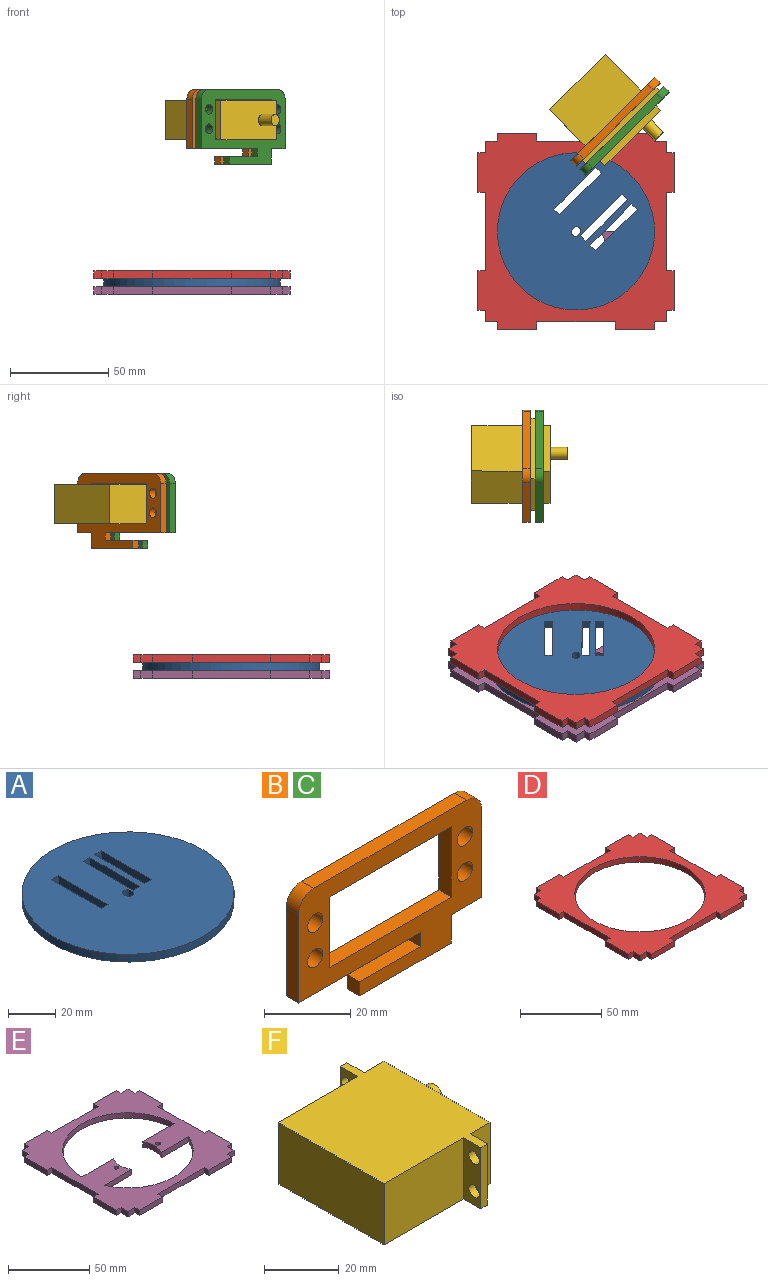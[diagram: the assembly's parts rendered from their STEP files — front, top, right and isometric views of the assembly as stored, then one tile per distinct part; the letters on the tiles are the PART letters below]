
ASSEMBLY  parts=6 mates=4
PART A: 19 faces, bbox 90x90x4 mm
  f0: plane 90x90mm, normal (0,0,1), area 5984.1mm2, adj f2,f3,f4,f5,f6,f7,f8,f9
  f1: plane 90x90mm, normal (0,0,-1), area 5984.1mm2, adj f2,f3,f4,f5,f6,f7,f8,f9
  f2: cylinder r=2.5mm len=4mm, axis (0,0,-1), area 18.5mm2, adj f0,f1,f3,f6
  f3: plane 4x3mm, normal (1,0,0), area 12mm2, adj f0,f1,f2,f4
  f4: cylinder r=2.5mm len=4mm, axis (0,0,-1), area 18.5mm2, adj f0,f1,f3,f6
  f5: cylinder r=45mm len=90mm, axis (0,0,-1), area 1131mm2, adj f0,f1
  f6: plane 4x3mm, normal (-1,0,0), area 12mm2, adj f0,f1,f2,f4
  f7: plane 4x4mm, normal (0,-1,0), area 16mm2, adj f0,f1,f8,f10
  f8: plane 30x4mm, normal (1,0,0), area 120mm2, adj f0,f1,f7,f9
  f9: plane 4x4mm, normal (0,1,0), area 16mm2, adj f0,f1,f8,f10
  f10: plane 30x4mm, normal (-1,0,0), area 120mm2, adj f0,f1,f7,f9
  f11: plane 4x4mm, normal (0,-1,0), area 16mm2, adj f0,f1,f12,f14
  f12: plane 30x4mm, normal (1,0,0), area 120mm2, adj f0,f1,f11,f13
  f13: plane 4x4mm, normal (0,1,0), area 16mm2, adj f0,f1,f12,f14
  f14: plane 30x4mm, normal (-1,0,0), area 120mm2, adj f0,f1,f11,f13
  f15: plane 30x4mm, normal (-1,0,0), area 120mm2, adj f0,f1,f16,f18
  f16: plane 4x4mm, normal (0,-1,0), area 16mm2, adj f0,f1,f15,f17
  f17: plane 30x4mm, normal (1,0,0), area 120mm2, adj f0,f1,f16,f18
  f18: plane 4x4mm, normal (0,1,0), area 16mm2, adj f0,f1,f15,f17
PART B: 22 faces, bbox 60x4x38 mm
  f0: plane 50x4mm, normal (0,0,1), area 200mm2, adj f1,f17,f20,f21
  f1: cylinder r=5mm len=5mm, axis (0,1,0), area 31.4mm2, adj f0,f2,f20,f21
  f2: plane 25x4mm, normal (-1,0,0), area 100mm2, adj f1,f3,f20,f21
  f3: plane 40x4mm, normal (0,0,-1), area 160mm2, adj f2,f4,f20,f21
  f4: plane 4x4mm, normal (-1,0,0), area 16mm2, adj f3,f5,f20,f21
  f5: plane 20x4mm, normal (0,0,1), area 80mm2, adj f4,f6,f20,f21
  f6: plane 4x4mm, normal (-1,0,0), area 16mm2, adj f5,f7,f20,f21
  f7: plane 30x4mm, normal (0,0,-1), area 120mm2, adj f6,f8,f20,f21
  f8: plane 8x4mm, normal (1,0,0), area 32mm2, adj f7,f9,f20,f21
  f9: plane 10x4mm, normal (0,0,-1), area 40mm2, adj f8,f10,f20,f21
  f10: plane 25x4mm, normal (1,0,0), area 100mm2, adj f9,f17,f20,f21
  f11: plane 20x4mm, normal (1,0,0), area 80mm2, adj f12,f18,f20,f21
  f12: plane 40x4mm, normal (0,0,-1), area 160mm2, adj f11,f13,f20,f21
  f13: plane 20x4mm, normal (-1,0,0), area 80mm2, adj f12,f18,f20,f21
  f14: cylinder r=2.5mm len=5mm, axis (0,1,0), area 62.8mm2, adj f20,f21
  f15: cylinder r=2.5mm len=5mm, axis (0,1,0), area 62.8mm2, adj f20,f21
  f16: cylinder r=2.5mm len=5mm, axis (0,1,0), area 62.8mm2, adj f20,f21
  f17: cylinder r=5mm len=5mm, axis (0,1,0), area 31.4mm2, adj f0,f10,f20,f21
  f18: plane 40x4mm, normal (0,0,1), area 160mm2, adj f11,f13,f20,f21
  f19: cylinder r=2.5mm len=5mm, axis (0,1,0), area 62.8mm2, adj f20,f21
  f20: plane 60x38mm, normal (0,-1,0), area 1070.7mm2, adj f0,f1,f2,f3,f4,f5,f6,f7
  f21: plane 60x38mm, normal (0,1,0), area 1070.7mm2, adj f0,f1,f2,f3,f4,f5,f6,f7
PART C: same geometry as B
PART D: 39 faces, bbox 100x100x4 mm
  f0: cylinder r=40mm len=80mm, axis (0,0,-1), area 1005.3mm2, adj f37,f38
  f1: plane 4x4mm, normal (0,-1,0), area 16mm2, adj f2,f36,f37,f38
  f2: plane 40x4mm, normal (-1,0,0), area 160mm2, adj f1,f3,f37,f38
  f3: plane 4x4mm, normal (0,1,0), area 16mm2, adj f2,f4,f37,f38
  f4: plane 20x4mm, normal (-1,0,0), area 80mm2, adj f3,f5,f37,f38
  f5: plane 4x4mm, normal (0,-1,0), area 16mm2, adj f4,f6,f37,f38
  f6: plane 6x4mm, normal (-1,0,0), area 24mm2, adj f5,f7,f37,f38
  f7: plane 6x4mm, normal (0,-1,0), area 24mm2, adj f6,f8,f37,f38
  f8: plane 4x4mm, normal (-1,0,0), area 16mm2, adj f7,f9,f37,f38
  f9: plane 20x4mm, normal (0,-1,0), area 80mm2, adj f8,f10,f37,f38
  f10: plane 4x4mm, normal (1,0,0), area 16mm2, adj f9,f11,f37,f38
  f11: plane 40x4mm, normal (0,-1,0), area 160mm2, adj f10,f12,f37,f38
  f12: plane 4x4mm, normal (-1,0,0), area 16mm2, adj f11,f13,f37,f38
  f13: plane 20x4mm, normal (0,-1,0), area 80mm2, adj f12,f14,f37,f38
  f14: plane 4x4mm, normal (1,0,0), area 16mm2, adj f13,f15,f37,f38
  f15: plane 6x4mm, normal (0,-1,0), area 24mm2, adj f14,f16,f37,f38
  f16: plane 6x4mm, normal (1,0,0), area 24mm2, adj f15,f17,f37,f38
  f17: plane 4x4mm, normal (0,-1,0), area 16mm2, adj f16,f18,f37,f38
  f18: plane 20x4mm, normal (1,0,0), area 80mm2, adj f17,f19,f37,f38
  f19: plane 4x4mm, normal (0,1,0), area 16mm2, adj f18,f20,f37,f38
  f20: plane 40x4mm, normal (1,0,0), area 160mm2, adj f19,f21,f37,f38
  f21: plane 4x4mm, normal (0,-1,0), area 16mm2, adj f20,f22,f37,f38
  f22: plane 20x4mm, normal (1,0,0), area 80mm2, adj f21,f23,f37,f38
  f23: plane 4x4mm, normal (0,1,0), area 16mm2, adj f22,f24,f37,f38
  f24: plane 6x4mm, normal (1,0,0), area 24mm2, adj f23,f25,f37,f38
  f25: plane 6x4mm, normal (0,1,0), area 24mm2, adj f24,f26,f37,f38
  f26: plane 4x4mm, normal (1,0,0), area 16mm2, adj f25,f27,f37,f38
  f27: plane 20x4mm, normal (0,1,0), area 80mm2, adj f26,f28,f37,f38
  f28: plane 4x4mm, normal (-1,0,0), area 16mm2, adj f27,f29,f37,f38
  f29: plane 40x4mm, normal (0,1,0), area 160mm2, adj f28,f30,f37,f38
  f30: plane 4x4mm, normal (1,0,0), area 16mm2, adj f29,f31,f37,f38
  f31: plane 20x4mm, normal (0,1,0), area 80mm2, adj f30,f32,f37,f38
  f32: plane 4x4mm, normal (-1,0,0), area 16mm2, adj f31,f33,f37,f38
  f33: plane 6x4mm, normal (0,1,0), area 24mm2, adj f32,f34,f37,f38
  f34: plane 6x4mm, normal (-1,0,0), area 24mm2, adj f33,f35,f37,f38
  f35: plane 4x4mm, normal (0,1,0), area 16mm2, adj f34,f36,f37,f38
  f36: plane 20x4mm, normal (-1,0,0), area 80mm2, adj f1,f35,f37,f38
  f37: plane 100x100mm, normal (0,0,1), area 4077.5mm2, adj f0,f1,f2,f3,f4,f5,f6,f7
  f38: plane 100x100mm, normal (0,0,-1), area 4077.5mm2, adj f0,f1,f2,f3,f4,f5,f6,f7
PART E: 48 faces, bbox 100x100x4 mm
  f0: cylinder r=40mm len=80mm, axis (0,0,-1), area 502.7mm2, adj f1,f43,f46,f47
  f1: plane 27.31x4mm, normal (0,1,0), area 109.2mm2, adj f0,f2,f46,f47
  f2: cylinder r=15mm len=16mm, axis (0,0,-1), area 67.5mm2, adj f1,f3,f46,f47
  f3: plane 23.97x4mm, normal (0,-1,0), area 95.9mm2, adj f2,f4,f46,f47
  f4: cylinder r=40mm len=73.32mm, axis (0,0,-1), area 371mm2, adj f3,f5,f46,f47
  f5: plane 23.97x4mm, normal (0,-1,0), area 95.9mm2, adj f4,f6,f46,f47
  f6: cylinder r=15mm len=16mm, axis (0,0,-1), area 67.5mm2, adj f5,f43,f46,f47
  f7: plane 4x4mm, normal (0,-1,0), area 16mm2, adj f8,f44,f46,f47
  f8: plane 40x4mm, normal (-1,0,0), area 160mm2, adj f7,f9,f46,f47
  f9: plane 4x4mm, normal (0,1,0), area 16mm2, adj f8,f10,f46,f47
  f10: plane 20x4mm, normal (-1,0,0), area 80mm2, adj f9,f11,f46,f47
  f11: plane 4x4mm, normal (0,-1,0), area 16mm2, adj f10,f12,f46,f47
  f12: plane 6x4mm, normal (-1,0,0), area 24mm2, adj f11,f13,f46,f47
  f13: plane 6x4mm, normal (0,-1,0), area 24mm2, adj f12,f14,f46,f47
  f14: plane 4x4mm, normal (-1,0,0), area 16mm2, adj f13,f15,f46,f47
  f15: plane 20x4mm, normal (0,-1,0), area 80mm2, adj f14,f16,f46,f47
  f16: plane 4x4mm, normal (1,0,0), area 16mm2, adj f15,f17,f46,f47
  f17: plane 40x4mm, normal (0,-1,0), area 160mm2, adj f16,f18,f46,f47
  f18: plane 4x4mm, normal (-1,0,0), area 16mm2, adj f17,f19,f46,f47
  f19: plane 20x4mm, normal (0,-1,0), area 80mm2, adj f18,f20,f46,f47
  f20: plane 4x4mm, normal (1,0,0), area 16mm2, adj f19,f21,f46,f47
  f21: plane 6x4mm, normal (0,-1,0), area 24mm2, adj f20,f22,f46,f47
  f22: plane 6x4mm, normal (1,0,0), area 24mm2, adj f21,f23,f46,f47
  f23: plane 4x4mm, normal (0,-1,0), area 16mm2, adj f22,f24,f46,f47
  f24: plane 20x4mm, normal (1,0,0), area 80mm2, adj f23,f25,f46,f47
  f25: plane 4x4mm, normal (0,1,0), area 16mm2, adj f24,f26,f46,f47
  f26: plane 40x4mm, normal (1,0,0), area 160mm2, adj f25,f27,f46,f47
  f27: plane 4x4mm, normal (0,-1,0), area 16mm2, adj f26,f28,f46,f47
  f28: plane 20x4mm, normal (1,0,0), area 80mm2, adj f27,f29,f46,f47
  f29: plane 4x4mm, normal (0,1,0), area 16mm2, adj f28,f30,f46,f47
  f30: plane 6x4mm, normal (1,0,0), area 24mm2, adj f29,f31,f46,f47
  f31: plane 6x4mm, normal (0,1,0), area 24mm2, adj f30,f32,f46,f47
  f32: plane 4x4mm, normal (1,0,0), area 16mm2, adj f31,f33,f46,f47
  f33: plane 20x4mm, normal (0,1,0), area 80mm2, adj f32,f34,f46,f47
  f34: plane 4x4mm, normal (-1,0,0), area 16mm2, adj f33,f35,f46,f47
  f35: plane 40x4mm, normal (0,1,0), area 160mm2, adj f34,f36,f46,f47
  f36: plane 4x4mm, normal (1,0,0), area 16mm2, adj f35,f37,f46,f47
  f37: plane 20x4mm, normal (0,1,0), area 80mm2, adj f36,f38,f46,f47
  f38: plane 4x4mm, normal (-1,0,0), area 16mm2, adj f37,f39,f46,f47
  f39: plane 6x4mm, normal (0,1,0), area 24mm2, adj f38,f40,f46,f47
  f40: plane 6x4mm, normal (-1,0,0), area 24mm2, adj f39,f41,f46,f47
  f41: plane 4x4mm, normal (0,1,0), area 16mm2, adj f40,f44,f46,f47
  f42: cylinder r=1.5mm len=4mm, axis (0,0,-1), area 37.7mm2, adj f46,f47
  f43: plane 27.31x4mm, normal (0,1,0), area 109.2mm2, adj f0,f6,f46,f47
  f44: plane 20x4mm, normal (-1,0,0), area 80mm2, adj f7,f41,f46,f47
  f45: cylinder r=1.5mm len=4mm, axis (0,0,-1), area 37.7mm2, adj f46,f47
  f46: plane 100x100mm, normal (0,0,1), area 4852.2mm2, adj f0,f1,f2,f3,f4,f5,f6,f7
  f47: plane 100x100mm, normal (0,0,-1), area 4852.2mm2, adj f0,f1,f2,f3,f4,f5,f6,f7
PART F: 20 faces, bbox 49x53x20 mm
  f0: plane 30x20mm, normal (0,-1,0), area 600mm2, adj f6,f8,f9,f13
  f1: plane 20x6.5mm, normal (-1,0,0), area 104.9mm2, adj f3,f8,f9,f10,f11,f12
  f2: plane 20x6.5mm, normal (1,0,0), area 104.9mm2, adj f5,f8,f9,f10,f11,f12
  f3: plane 30x20mm, normal (0,1,0), area 600mm2, adj f1,f6,f8,f9
  f4: plane 40x20mm, normal (1,0,0), area 771.7mm2, adj f5,f7,f8,f9,f18
  f5: plane 20x7.5mm, normal (0,1,0), area 150mm2, adj f2,f4,f8,f9
  f6: plane 40x20mm, normal (-1,0,0), area 800mm2, adj f0,f3,f8,f9
  f7: plane 20x7.5mm, normal (0,-1,0), area 150mm2, adj f4,f8,f9,f14
  f8: plane 53x40mm, normal (0,0,1), area 1632.5mm2, adj f0,f1,f2,f3,f4,f5,f6,f7
  f9: plane 53x40mm, normal (0,0,-1), area 1632.5mm2, adj f0,f1,f2,f3,f4,f5,f6,f7
  f10: plane 20x2.5mm, normal (0,1,0), area 50mm2, adj f1,f2,f8,f9
  f11: cylinder r=2mm len=4mm, axis (1,0,0), area 31.4mm2, adj f1,f2
  f12: cylinder r=2mm len=4mm, axis (1,0,0), area 31.4mm2, adj f1,f2
  f13: plane 20x6.5mm, normal (-1,0,0), area 104.9mm2, adj f0,f8,f9,f15,f16,f17
  f14: plane 20x6.5mm, normal (1,0,0), area 104.9mm2, adj f7,f8,f9,f15,f16,f17
  f15: plane 20x2.5mm, normal (0,-1,0), area 50mm2, adj f8,f9,f13,f14
  f16: cylinder r=2mm len=4mm, axis (1,0,0), area 31.4mm2, adj f13,f14
  f17: cylinder r=2mm len=4mm, axis (1,0,0), area 31.4mm2, adj f13,f14
  f18: cylinder r=3mm len=9mm, axis (-1,0,0), area 169.6mm2, adj f4,f19
  f19: plane 6x6mm, normal (1,0,0), area 28.3mm2, adj f18
PLACE A rot(axis=(0,0,-1),45.3deg) t=(103.96,68.5,-6.29)mm
PLACE B rot(axis=(0,0,1),44.7deg) t=(122.68,125.6,59.95)mm
PLACE C rot(axis=(0,0,1),44.7deg) t=(127.25,120.99,59.95)mm
PLACE D t=(103.96,68.5,-7.29)mm
PLACE E t=(103.96,68.5,-6.29)mm fixed
PLACE F rot(axis=(0,0,-1),45.3deg) t=(118.81,130.21,82.45)mm
MATE revolute E.f0 <-> A.f5  axis (0,0,1) through (103.96,68.5,-2.29)mm
MATE fastened B.f16 <-> F.f11  axis (0.7,-0.71,0) through (142.89,140.01,87.95)mm
MATE revolute D.f0 <-> A.f5  axis (0,0,-1) through (103.96,68.5,1.71)mm
MATE fastened C.f16 <-> F.f11  axis (-0.7,0.71,0) through (144.65,138.23,87.95)mm
